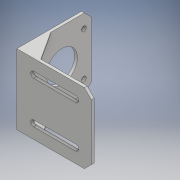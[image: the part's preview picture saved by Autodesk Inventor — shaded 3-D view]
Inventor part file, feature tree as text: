
AUTODESK INVENTOR PART (.ipt)
format: ipt  version: 2018 (Build 220112000, 112)  size: 187,904 bytes
history: native  units: mm
features: extrude x6, sketch x6, mirror x1, projected_geometry x1
ambient origin geometry x8: Origin, YZ Plane, XZ Plane, XY Plane, X Axis, Y Axis, Z Axis, Center Point
bodies: Solid1 (feature_tree)
feature tree (14):
  extrude  "Extrusion1"  Depth=2.0mm
  extrude  "Extrusion2"  Depth=53.0mm
  extrude  "Extrusion3"  Depth=50.0mm
  extrude  "Extrusion4"  Depth=31.0mm
  extrude  "Extrusion5"  Depth=21.0mm
  extrude  "Extrusion6"  TaperAngle=45.0deg  [1 undecoded]
  mirror  "Mirror1"
  sketch  "Sketch1"  dims[d1=51.0mm d2=2.0mm]
  sketch  "Sketch2"  dims[d4=2.0mm d5=53.0mm]
  sketch  "Sketch3"  dims[d6=50.0mm d7=0.0mm d8=22.1mm]
  sketch  "Sketch4"  dims[d9=3.5mm d10=31.0mm]
  sketch  "Sketch5"  dims[d11=31.0mm d12=21.0mm]
  projected_geometry  "Projected Loop1"
  sketch  "Sketch6"  dims[d13=50.0mm d14=0.0mm d15=45.0deg d16=5.0mm d17=50.0mm d18=0.0mm d19=4.2mm d20=30.0mm d21=30.0mm d22=4.2mm d23=11.0mm d24=50.0mm d25=0.0mm d26=5.0mm d27=5.0mm d28=50.0mm d29=0.0mm d30=13.0mm d31=20.0mm d32=1.0mm d33=0.0mm]
note: 1 required parameter value undecoded (feature->parameter linkage not recoverable at this tier; creation-order binding heuristic only, values carry confidence <= 0.55)
